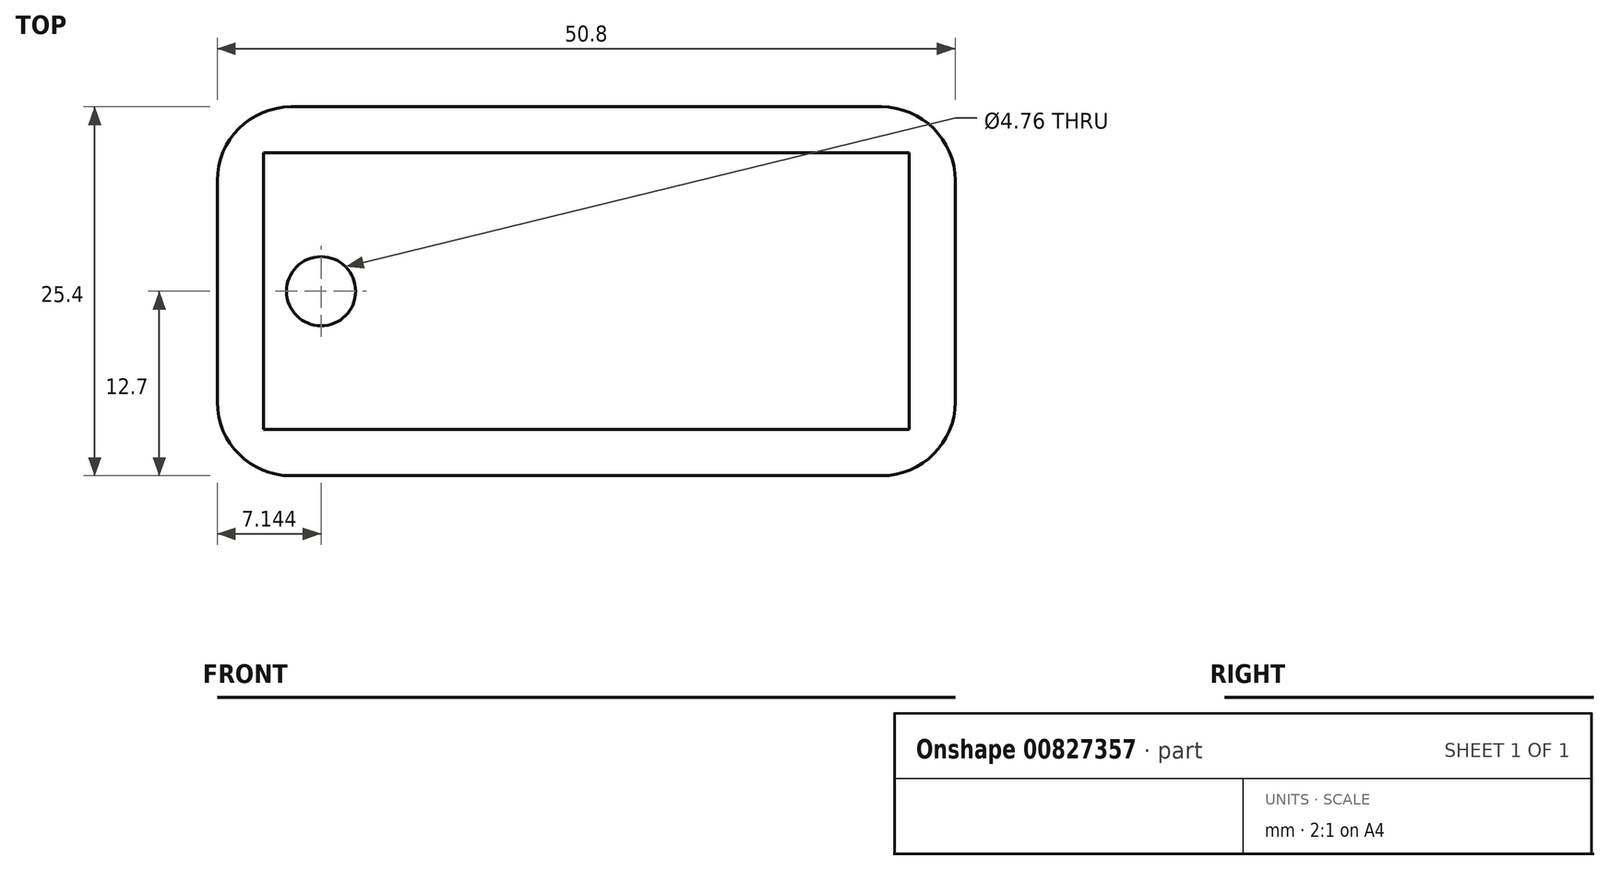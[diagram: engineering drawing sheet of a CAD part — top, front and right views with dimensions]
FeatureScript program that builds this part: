
annotation { "Feature Type Name" : "Feature", "Feature Type Description" : "" }
export const myFeature = defineFeature(function(context is Context, id is Id, definition is map)
    precondition{}
    {
        {
            var Q0;
            Q0=qCreatedBy(makeId("Top.planeOp"),FACE);
            var sketch = newSketch(context, id + "F0", { "sketchPlane" : qUnion([Q0])});
            skLineSegment(sketch, "E0.bottom", {"start": v(0, 0) * mm, "end": v(50.8, 0) * mm});
            skLineSegment(sketch, "E0.top", {"start": v(0, 25.4) * mm, "end": v(50.8, 25.4) * mm});
            skLineSegment(sketch, "E0.left", {"start": v(0, 0) * mm, "end": v(0, 25.4) * mm});
            skLineSegment(sketch, "E0.right", {"start": v(50.8, 0) * mm, "end": v(50.8, 25.4) * mm});
            skCircle(sketch, "E1", {"center": v(7.14, 12.7) * mm, "radius": 2.38 * mm});
            skPoint(sketch, "E2", {"position": v(0, 12.7) * mm});
            skLineSegment(sketch, "E3.bottom", {"start": v(3.17, 22.23) * mm, "end": v(47.63, 22.23) * mm});
            skLineSegment(sketch, "E3.top", {"start": v(3.18, 3.18) * mm, "end": v(47.63, 3.18) * mm});
            skLineSegment(sketch, "E3.left", {"start": v(3.17, 22.23) * mm, "end": v(3.18, 3.18) * mm});
            skLineSegment(sketch, "E3.right", {"start": v(47.63, 22.23) * mm, "end": v(47.63, 3.18) * mm});
            skSolve(sketch);
        }
        {
            var Q0;
            Q0=makeQuery(id+"F0.imprint","IMPRINT",FACE,{"disambiguationData":[TD([[makeQuery(id+"F0.imprint","IMPRINT",EDGE,{"derivedFrom":sQuery(id+"F0.wireOp",EDGE,"E1")}),-1.0]])]});
            extrude(context, id + "F1", {"entities" : qUnion([Q0]), "depth" : 1 / 406.4 * mm, "offsetDistance" : 25.4 * mm});
        }
        {
            var Q0;
            Q0 = qSketchRegion(id + "F0", true);
            extrude(context, id + "F2", {"entities" : qUnion([Q0]), "operationType" : NewBodyOperationType.ADD, "depth" : 1 / 203.2 * mm, "offsetDistance" : 25.4 * mm});
        }
        {
            var Q0;
            Q0=makeQuery(id+"F2.opExtrude","SWEPT_EDGE",EDGE,{"disambiguationData":[OSD([sQuery(id+"F0.wireOp",EDGE,"E0.bottom"),sQuery(id+"F0.wireOp",EDGE,"E0.right")])]});
            var Q1;
            Q1=makeQuery(id+"F2.opExtrude","SWEPT_EDGE",EDGE,{"disambiguationData":[OSD([sQuery(id+"F0.wireOp",EDGE,"E0.top"),sQuery(id+"F0.wireOp",EDGE,"E0.right")])]});
            var Q2;
            Q2=makeQuery(id+"F2.opExtrude","SWEPT_EDGE",EDGE,{"disambiguationData":[OSD([sQuery(id+"F0.wireOp",EDGE,"E0.bottom"),sQuery(id+"F0.wireOp",EDGE,"E0.left")])]});
            var Q3;
            Q3=makeQuery(id+"F2.opExtrude","SWEPT_EDGE",EDGE,{"disambiguationData":[OSD([sQuery(id+"F0.wireOp",EDGE,"E0.top"),sQuery(id+"F0.wireOp",EDGE,"E0.left")])]});
            fillet(context, id + "F3", {"entities" : qUnion([Q0, Q1, Q2, Q3]), "radius" : 5.08 * mm, "tangentPropagation" : true, "allowEdgeOverflow" : false});
        }
    });
